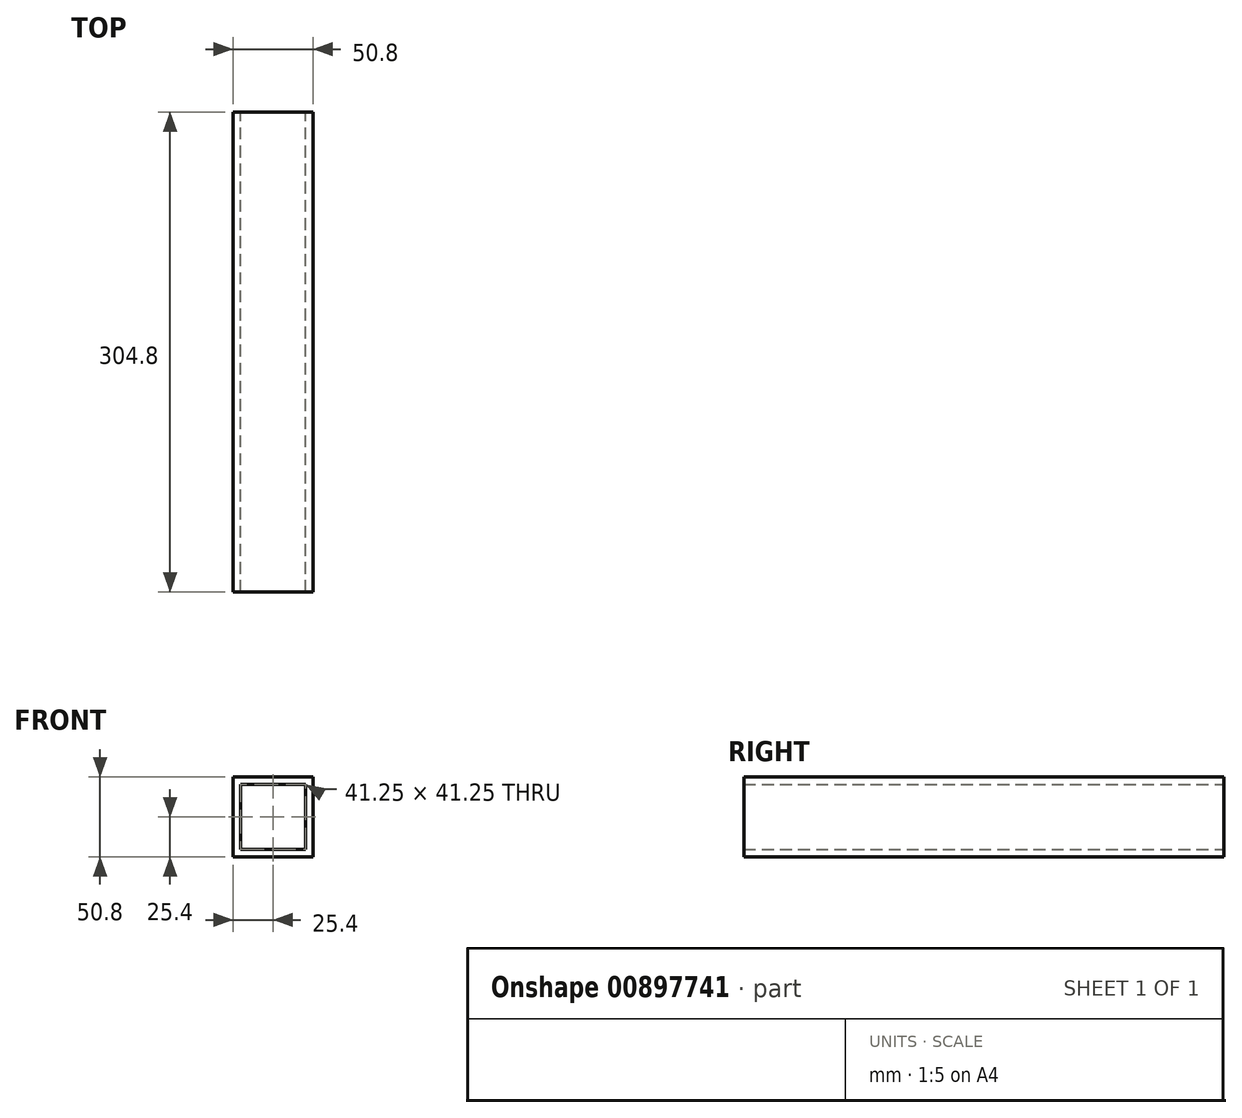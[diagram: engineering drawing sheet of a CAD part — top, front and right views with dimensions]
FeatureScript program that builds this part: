
annotation { "Feature Type Name" : "Feature", "Feature Type Description" : "" }
export const myFeature = defineFeature(function(context is Context, id is Id, definition is map)
    precondition{}
    {
        {
            var Q0;
            Q0=qCreatedBy(makeId("Front.planeOp"),FACE);
            var sketch = newSketch(context, id + "F0", { "sketchPlane" : qUnion([Q0])});
            skLineSegment(sketch, "E0.bottom", {"start": v(0, 0) * mm, "end": v(50.8, 0) * mm});
            skLineSegment(sketch, "E0.top", {"start": v(0, 50.8) * mm, "end": v(50.8, 50.8) * mm});
            skLineSegment(sketch, "E0.left", {"start": v(0, 0) * mm, "end": v(0, 50.8) * mm});
            skLineSegment(sketch, "E0.right", {"start": v(50.8, 0) * mm, "end": v(50.8, 50.8) * mm});
            skLineSegment(sketch, "E1.bottom", {"start": v(4.78, 4.78) * mm, "end": v(46.02, 4.78) * mm});
            skLineSegment(sketch, "E1.top", {"start": v(4.78, 46.02) * mm, "end": v(46.02, 46.02) * mm});
            skLineSegment(sketch, "E1.left", {"start": v(4.78, 4.78) * mm, "end": v(4.78, 46.02) * mm});
            skLineSegment(sketch, "E1.right", {"start": v(46.02, 4.78) * mm, "end": v(46.02, 46.02) * mm});
            skSolve(sketch);
        }
        {
            var Q0;
            Q0 = qSketchRegion(id + "F0", true);
            extrude(context, id + "F1", {"entities" : qUnion([Q0]), "depth" : 304.8 * mm, "offsetDistance" : 25.4 * mm});
        }
        {
            var Q0;
            Q0=makeQuery(id+"F1.opExtrude","SWEPT_FACE",FACE,{"disambiguationData":[OSD([sQuery(id+"F0.wireOp",EDGE,"E0.right")])]});
            var sketch = newSketch(context, id + "F2", { "sketchPlane" : qUnion([Q0])});
            skPoint(sketch, "E2", {"position": v(-254, 25.4) * mm});
            skSolve(sketch);
        }
    });
